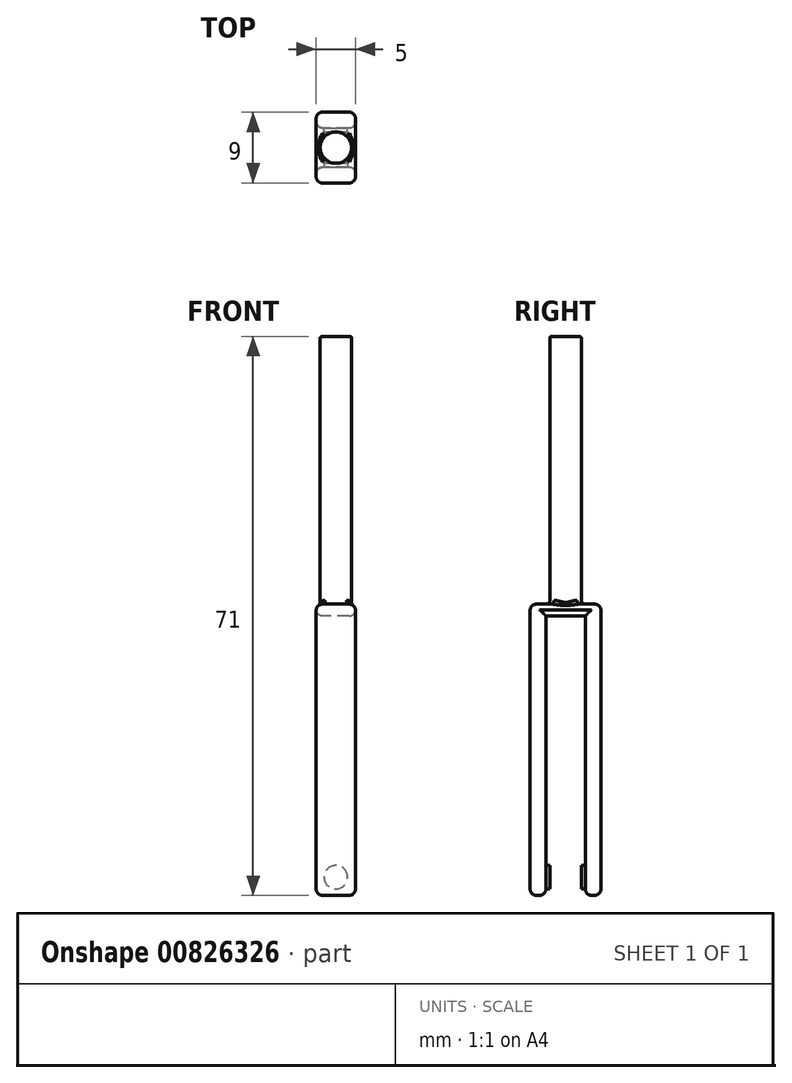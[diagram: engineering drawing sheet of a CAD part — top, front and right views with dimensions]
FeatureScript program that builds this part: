
annotation { "Feature Type Name" : "Feature", "Feature Type Description" : "" }
export const myFeature = defineFeature(function(context is Context, id is Id, definition is map)
    precondition{}
    {
        {
            var Q0;
            Q0=qCreatedBy(makeId("Front.planeOp"),FACE);
            var sketch = newSketch(context, id + "F0", { "sketchPlane" : qUnion([Q0])});
            skLineSegment(sketch, "E0", {"start": v(-41.6, 28) * mm, "end": v(-41.6, 0) * mm});
            skLineSegment(sketch, "E1", {"start": v(-36.6, 28) * mm, "end": v(-41.6, 28) * mm});
            skLineSegment(sketch, "E2", {"start": v(-41.6, 0) * mm, "end": v(-50.78, 0) * mm});
            skLineSegment(sketch, "E3", {"start": v(-41.6, 0) * mm, "end": v(-41.6, -9) * mm});
            skLineSegment(sketch, "E4", {"start": v(-41.6, -9) * mm, "end": v(-36.6, -9) * mm});
            skLineSegment(sketch, "E5", {"start": v(-36.6, -9) * mm, "end": v(-36.6, 28) * mm});
            skSolve(sketch);
        }
        {
            var Q0;
            Q0=makeQuery(id+"F0.imprint","IMPRINT",FACE,{"disambiguationData":[TD([[makeQuery(id+"F0.imprint","IMPRINT",EDGE,{"derivedFrom":sQuery(id+"F0.wireOp",EDGE,"E0")}),1.0]])]});
            extrude(context, id + "F1", {"entities" : qUnion([Q0]), "oppositeDirection" : true, "depth" : 2 * mm, "offsetDistance" : 25 * mm});
        }
        {
            var Q0;
            Q0=qCreatedBy(makeId("Front.planeOp"),FACE);
            cPlane(context, id + "F2", {"entities" : qUnion([Q0]), "cplaneType" : CPlaneType.OFFSET, "offset" : 2.5 * mm, "width" : 150 * mm, "height" : 150 * mm});
        }
        {
            var Q0;
            Q0=qCreatedBy(makeId("Top.planeOp"),FACE);
            cPlane(context, id + "F3", {"entities" : qUnion([Q0]), "cplaneType" : CPlaneType.OFFSET, "offset" : 27 * mm, "width" : 150 * mm, "height" : 150 * mm});
        }
        {
            var Q0;
            Q0=makeQuery(id+"F1.opExtrude","CAP_FACE",FACE,{"disambiguationData":[OSD([sQuery(id+"F0.wireOp",EDGE,"E0"),sQuery(id+"F0.wireOp",EDGE,"E1"),sQuery(id+"F0.wireOp",EDGE,"E3"),sQuery(id+"F0.wireOp",EDGE,"E4"),sQuery(id+"F0.wireOp",EDGE,"E5")])],"isStart":true});
            var sketch = newSketch(context, id + "F4", { "sketchPlane" : qUnion([Q0])});
            skPoint(sketch, "E6.trimOffspring.end.orphan", {"position": v(-36.6, -12.26) * mm});
            skPoint(sketch, "E7.start.orphan", {"position": v(-41.6, -10.83) * mm});
            skPoint(sketch, "E8.trimOffspring.end.orphan", {"position": v(-36.6, 30.02) * mm});
            skPoint(sketch, "E9.start.orphan", {"position": v(-41.6, 25.12) * mm});
            skPoint(sketch, "E10.center.orphan", {"position": v(-39.1, 27.57) * mm});
            skLineSegment(sketch, "E11.bottom", {"start": v(-36.6, 30.02) * mm, "end": v(-36.6, 30.02) * mm});
            skLineSegment(sketch, "E11.top", {"start": v(-36.6, 26.5) * mm, "end": v(-36.6, 26.5) * mm});
            skLineSegment(sketch, "E11.left", {"start": v(-36.6, 30.02) * mm, "end": v(-36.6, 26.5) * mm});
            skLineSegment(sketch, "E11.right", {"start": v(-36.6, 30.02) * mm, "end": v(-36.6, 26.5) * mm});
            skLineSegment(sketch, "E12.right", {"start": v(-41.6, 30.02) * mm, "end": v(-41.6, 30.02) * mm});
            skLineSegment(sketch, "E13.bottom", {"start": v(-41.6, 26.5) * mm, "end": v(-41.6, 26.5) * mm});
            skLineSegment(sketch, "E14", {"start": v(-41.6, 26.5) * mm, "end": v(-36.6, 26.5) * mm});
            skLineSegment(sketch, "E15", {"start": v(-36.6, 26.5) * mm, "end": v(-36.6, 28) * mm});
            skLineSegment(sketch, "E16", {"start": v(-36.6, 28) * mm, "end": v(-41.6, 28) * mm});
            skLineSegment(sketch, "E17", {"start": v(-41.6, 28) * mm, "end": v(-41.6, 26.5) * mm});
            skPoint(sketch, "E18.center.orphan", {"position": v(-39.1, -11.55) * mm});
            skCircle(sketch, "E19", {"center": v(-39.1, -6.69) * mm, "radius": 1.5 * mm});
            skPoint(sketch, "E20.orphan", {"position": v(-41.6, -6.69) * mm});
            skPoint(sketch, "E21.end.orphan", {"position": v(-36.6, -6.69) * mm});
            skSolve(sketch);
        }
        {
            var Q0;
            Q0=makeQuery(id+"F1.opExtrude","CAP_EDGE",EDGE,{"disambiguationData":[OSD([sQuery(id+"F0.wireOp",EDGE,"E5")])],"isStart":false});
            var Q1;
            Q1=makeQuery(id+"F1.opExtrude","CAP_EDGE",EDGE,{"disambiguationData":[OSD([sQuery(id+"F0.wireOp",EDGE,"E4")])],"isStart":false});
            var Q2;
            Q2=makeQuery(id+"F1.opExtrude","CAP_EDGE",EDGE,{"disambiguationData":[OSD([sQuery(id+"F0.wireOp",EDGE,"E4")])],"isStart":true});
            var Q3;
            Q3=makeQuery(id+"F1.opExtrude","CAP_EDGE",EDGE,{"disambiguationData":[OSD([sQuery(id+"F0.wireOp",EDGE,"E5")])],"isStart":true});
            var Q4;
            Q4=makeQuery(id+"F1.opExtrude","CAP_EDGE",EDGE,{"disambiguationData":[OSD([sQuery(id+"F0.wireOp",EDGE,"E0"),sQuery(id+"F0.wireOp",EDGE,"E3")])],"isStart":true});
            var Q5;
            Q5=makeQuery(id+"F1.opExtrude","CAP_EDGE",EDGE,{"disambiguationData":[OSD([sQuery(id+"F0.wireOp",EDGE,"E0"),sQuery(id+"F0.wireOp",EDGE,"E3")])],"isStart":false});
            var Q6;
            Q6=makeQuery(id+"F1.opExtrude","CAP_EDGE",EDGE,{"disambiguationData":[OSD([sQuery(id+"F0.wireOp",EDGE,"E1")])],"isStart":false});
            var Q7;
            Q7=makeQuery(id+"F1.opExtrude","CAP_EDGE",EDGE,{"disambiguationData":[OSD([sQuery(id+"F0.wireOp",EDGE,"E1")])],"isStart":true});
            var Q8;
            Q8=makeQuery(id+"F1.opExtrude","SWEPT_EDGE",EDGE,{"disambiguationData":[OSD([sQuery(id+"F0.wireOp",EDGE,"E0"),sQuery(id+"F0.wireOp",EDGE,"E1")])]});
            var Q9;
            Q9=makeQuery(id+"F1.opExtrude","SWEPT_EDGE",EDGE,{"disambiguationData":[OSD([sQuery(id+"F0.wireOp",EDGE,"E1"),sQuery(id+"F0.wireOp",EDGE,"E5")])]});
            var Q10;
            Q10=makeQuery(id+"F1.opExtrude","SWEPT_EDGE",EDGE,{"disambiguationData":[OSD([sQuery(id+"F0.wireOp",EDGE,"E4"),sQuery(id+"F0.wireOp",EDGE,"E5")])]});
            var Q11;
            Q11=makeQuery(id+"F1.opExtrude","SWEPT_EDGE",EDGE,{"disambiguationData":[OSD([sQuery(id+"F0.wireOp",EDGE,"E3"),sQuery(id+"F0.wireOp",EDGE,"E4")])]});
            fillet(context, id + "F5", {"entities" : qUnion([Q0, Q1, Q2, Q3, Q4, Q5, Q6, Q7, Q8, Q9, Q10, Q11]), "radius" : 0.8 * mm, "tangentPropagation" : true, "allowEdgeOverflow" : false});
        }
        {
            var Q0;
            Q0=makeQuery(id+"F1.opExtrude","SWEPT_BODY",BODY,{"disambiguationData":[OSD([sQuery(id+"F0.wireOp",EDGE,"E0"),sQuery(id+"F0.wireOp",EDGE,"E1"),sQuery(id+"F0.wireOp",EDGE,"E3"),sQuery(id+"F0.wireOp",EDGE,"E4"),sQuery(id+"F0.wireOp",EDGE,"E5")])]});
            var Q1;
            Q1=qCreatedBy(id+"F2.planeOp",FACE);
            mirror(context, id + "F6", {"operationType" : NewBodyOperationType.ADD, "entities" : qUnion([Q0]), "mirrorPlane" : qUnion([Q1])});
        }
        {
            var Q0;
            Q0=makeQuery(id+"F4.imprint","IMPRINT",FACE,{"disambiguationData":[TD([[makeQuery(id+"F4.imprint","IMPRINT",EDGE,{"derivedFrom":sQuery(id+"F4.wireOp",EDGE,"E14")}),1.0]])]});
            extrude(context, id + "F7", {"entities" : qUnion([Q0]), "depth" : 6 * mm, "offsetDistance" : 25 * mm});
        }
        {
            var Q0;
            Q0=makeQuery(id+"F7.opExtrude","SWEPT_BODY",BODY,{"disambiguationData":[OSD([sQuery(id+"F4.wireOp",EDGE,"E14"),sQuery(id+"F4.wireOp",EDGE,"E15"),sQuery(id+"F4.wireOp",EDGE,"E16"),sQuery(id+"F4.wireOp",EDGE,"E17")])]});
            var Q1;
            Q1=qCreatedBy(id+"F2.planeOp",FACE);
            mirror(context, id + "F8", {"entities" : qUnion([Q0]), "mirrorPlane" : qUnion([Q1])});
        }
        {
            var Q0;
            Q0=makeQuery(id+"F7.opExtrude","SWEPT_BODY",BODY,{"disambiguationData":[OSD([sQuery(id+"F4.wireOp",EDGE,"E14"),sQuery(id+"F4.wireOp",EDGE,"E15"),sQuery(id+"F4.wireOp",EDGE,"E16"),sQuery(id+"F4.wireOp",EDGE,"E17")])]});
            var Q1;
            Q1=makeQuery(id+"F8.opPattern","COPY",BODY,{"derivedFrom":makeQuery(id+"F7.opExtrude","SWEPT_BODY",BODY,{"disambiguationData":[OSD([sQuery(id+"F4.wireOp",EDGE,"E14"),sQuery(id+"F4.wireOp",EDGE,"E15"),sQuery(id+"F4.wireOp",EDGE,"E16"),sQuery(id+"F4.wireOp",EDGE,"E17")])]}),"instanceName":"1"});
            booleanBodies(context, id + "F9", {"operationType" : BooleanOperationType.UNION, "tools" : qUnion([Q0, Q1])});
        }
        {
            var Q0;
            {var subQ0=makeQuery(id+"F7.opExtrude","SWEPT_EDGE",EDGE,{"disambiguationData":[OSD([sQuery(id+"F4.wireOp",EDGE,"E16"),sQuery(id+"F4.wireOp",EDGE,"E17")])]});Q0=makeQuery(id+"F9.opBoolean","MERGE",EDGE,{"derivedFrom":[subQ0,makeQuery(id+"F8.opPattern","COPY",EDGE,{"derivedFrom":subQ0,"instanceName":"1"})]});}
            var Q1;
            {var subQ0=makeQuery(id+"F7.opExtrude","SWEPT_EDGE",EDGE,{"disambiguationData":[OSD([sQuery(id+"F0.wireOp",EDGE,"E0"),sQuery(id+"F0.wireOp",EDGE,"E3"),sQuery(id+"F4.wireOp",EDGE,"E14"),sQuery(id+"F4.wireOp",EDGE,"E17")])]});Q1=makeQuery(id+"F9.opBoolean","MERGE",EDGE,{"derivedFrom":[subQ0,makeQuery(id+"F8.opPattern","COPY",EDGE,{"derivedFrom":subQ0,"instanceName":"1"})]});}
            var Q2;
            {var subQ0=makeQuery(id+"F7.opExtrude","SWEPT_EDGE",EDGE,{"disambiguationData":[OSD([sQuery(id+"F0.wireOp",EDGE,"E5"),sQuery(id+"F4.wireOp",EDGE,"E14"),sQuery(id+"F4.wireOp",EDGE,"E15")])]});Q2=makeQuery(id+"F9.opBoolean","MERGE",EDGE,{"derivedFrom":[subQ0,makeQuery(id+"F8.opPattern","COPY",EDGE,{"derivedFrom":subQ0,"instanceName":"1"})]});}
            var Q3;
            {var subQ0=makeQuery(id+"F7.opExtrude","SWEPT_EDGE",EDGE,{"disambiguationData":[OSD([sQuery(id+"F4.wireOp",EDGE,"E15"),sQuery(id+"F4.wireOp",EDGE,"E16")])]});Q3=makeQuery(id+"F9.opBoolean","MERGE",EDGE,{"derivedFrom":[subQ0,makeQuery(id+"F8.opPattern","COPY",EDGE,{"derivedFrom":subQ0,"instanceName":"1"})]});}
            fillet(context, id + "F10", {"entities" : qUnion([Q0, Q1, Q2, Q3]), "radius" : 0.8 * mm, "tangentPropagation" : true, "allowEdgeOverflow" : false});
        }
        {
            var Q0;
            Q0=makeQuery(id+"F1.opExtrude","SWEPT_BODY",BODY,{"disambiguationData":[OSD([sQuery(id+"F0.wireOp",EDGE,"E0"),sQuery(id+"F0.wireOp",EDGE,"E1"),sQuery(id+"F0.wireOp",EDGE,"E3"),sQuery(id+"F0.wireOp",EDGE,"E4"),sQuery(id+"F0.wireOp",EDGE,"E5")])]});
            var Q1;
            Q1=makeQuery(id+"F6.opPattern","COPY",BODY,{"derivedFrom":makeQuery(id+"F1.opExtrude","SWEPT_BODY",BODY,{"disambiguationData":[OSD([sQuery(id+"F0.wireOp",EDGE,"E0"),sQuery(id+"F0.wireOp",EDGE,"E1"),sQuery(id+"F0.wireOp",EDGE,"E3"),sQuery(id+"F0.wireOp",EDGE,"E4"),sQuery(id+"F0.wireOp",EDGE,"E5")])]}),"instanceName":"1"});
            var Q2;
            Q2=makeQuery(id+"F7.opExtrude","SWEPT_BODY",BODY,{"disambiguationData":[OSD([sQuery(id+"F4.wireOp",EDGE,"E14"),sQuery(id+"F4.wireOp",EDGE,"E15"),sQuery(id+"F4.wireOp",EDGE,"E16"),sQuery(id+"F4.wireOp",EDGE,"E17")])]});
            booleanBodies(context, id + "F11", {"operationType" : BooleanOperationType.UNION, "tools" : qUnion([Q0, Q1, Q2])});
        }
        {
            var Q0;
            Q0=makeQuery(id+"F4.imprint","IMPRINT",FACE,{"disambiguationData":[TD([[makeQuery(id+"F4.imprint","IMPRINT",EDGE,{"derivedFrom":sQuery(id+"F4.wireOp",EDGE,"E19")}),1.0]])]});
            extrude(context, id + "F12", {"entities" : qUnion([Q0]), "operationType" : NewBodyOperationType.ADD, "depth" : 0.5 * mm, "offsetDistance" : 25 * mm});
        }
        {
            var Q0;
            Q0=makeQuery(id+"F1.opExtrude","SWEPT_BODY",BODY,{"disambiguationData":[OSD([sQuery(id+"F0.wireOp",EDGE,"E0"),sQuery(id+"F0.wireOp",EDGE,"E1"),sQuery(id+"F0.wireOp",EDGE,"E3"),sQuery(id+"F0.wireOp",EDGE,"E4"),sQuery(id+"F0.wireOp",EDGE,"E5")])]});
            var Q1;
            Q1=qCreatedBy(id+"F2.planeOp",FACE);
            mirror(context, id + "F13", {"operationType" : NewBodyOperationType.ADD, "entities" : qUnion([Q0]), "mirrorPlane" : qUnion([Q1])});
        }
        {
            var Q0;
            Q0=qCreatedBy(id+"F3.planeOp",FACE);
            var sketch = newSketch(context, id + "F14", { "sketchPlane" : qUnion([Q0])});
            skCircle(sketch, "E22", {"center": v(-39.1, -2.5) * mm, "radius": 2 * mm});
            skPoint(sketch, "E23.trimOffspring.end.orphan", {"position": v(-39.1, -6.2) * mm});
            skPoint(sketch, "E24.trimOffspring.end.orphan", {"position": v(-40.8, -6.2) * mm});
            skPoint(sketch, "E25.orphan", {"position": v(-41.6, -6.2) * mm});
            skPoint(sketch, "E26.start.orphan", {"position": v(-39.1, 1.2) * mm});
            skPoint(sketch, "E27.0.2.end.orphan", {"position": v(-41.6, 1.2) * mm});
            skPoint(sketch, "E28.0.2.end.orphan", {"position": v(-37.4, 1.2) * mm});
            skPoint(sketch, "E29.orphan", {"position": v(-36.6, 1.2) * mm});
            skPoint(sketch, "E28.0.1.start.orphan", {"position": v(-36.6, -6.2) * mm});
            skPoint(sketch, "E28.0.3.start.orphan", {"position": v(-37.4, -6.2) * mm});
            skPoint(sketch, "E30.trimOffspring.end.orphan", {"position": v(-40.8, 1.2) * mm});
            skSolve(sketch);
        }
        {
            var Q0;
            Q0 = qSketchRegion(id + "F14", true);
            extrude(context, id + "F15", {"entities" : qUnion([Q0]), "operationType" : NewBodyOperationType.ADD, "depth" : 35 * mm, "offsetDistance" : 25 * mm});
        }
        {
            var Q0;
            {var subQ0=sQuery(id+"F0.wireOp",EDGE,"E5");var subQ1=sQuery(id+"F0.wireOp",EDGE,"E1");var subQ2=makeQuery(id+"F5.opFillet","BLEND_FACE",FACE,{"disambiguationData":[OSD([subQ1,subQ0]),TDD([makeQuery(id+"F1.opExtrude","SWEPT_EDGE",EDGE,{"disambiguationData":[OSD([subQ1,subQ0])]})])]});Q0=makeQuery(id+"F15.boolean.opBoolean","INTERSECT",EDGE,{"derivedFrom":[makeQuery(id+"F11.opBoolean","MERGE",FACE,{"derivedFrom":[subQ2,makeQuery(id+"F6.opPattern","COPY",FACE,{"derivedFrom":subQ2,"instanceName":"1"}),makeQuery(id+"F10.opFillet","BLEND_FACE",FACE,{"disambiguationData":[OSD([sQuery(id+"F4.wireOp",EDGE,"E15"),sQuery(id+"F4.wireOp",EDGE,"E16")])]})]}),makeQuery(id+"F15.opExtrude","SWEPT_FACE",FACE,{"disambiguationData":[OSD([sQuery(id+"F14.wireOp",EDGE,"E22")])]})]});}
            var Q1;
            {var subQ1=sQuery(id+"F0.wireOp",EDGE,"E1");var subQ5=sQuery(id+"F4.wireOp",EDGE,"E16");var subQ6=makeQuery(id+"F7.opExtrude","SWEPT_FACE",FACE,{"disambiguationData":[OSD([subQ5])]});var subQ7=makeQuery(id+"F1.opExtrude","SWEPT_FACE",FACE,{"disambiguationData":[OSD([subQ1])]});Q1=makeQuery(id+"F15.boolean.opBoolean","SPLIT",FACE,{"disambiguationData":[TD([makeQuery(id+"F15.opExtrude","SWEPT_FACE",FACE,{"disambiguationData":[OSD([sQuery(id+"F14.wireOp",EDGE,"E22")])]})])],"derivedFrom":makeQuery(id+"F11.opBoolean","MERGE",FACE,{"derivedFrom":[subQ7,makeQuery(id+"F6.opPattern","COPY",FACE,{"derivedFrom":subQ7,"instanceName":"1"}),makeQuery(id+"F9.opBoolean","MERGE",FACE,{"derivedFrom":[subQ6,makeQuery(id+"F8.opPattern","COPY",FACE,{"derivedFrom":subQ6,"instanceName":"1"})]})]})});}
            fillet(context, id + "F16", {"entities" : qUnion([Q0, Q1]), "radius" : 0.5 * mm, "tangentPropagation" : true, "allowEdgeOverflow" : false});
        }
        {
            var Q0;
            Q0=makeQuery(id+"F15.opExtrude","CAP_FACE",FACE,{"disambiguationData":[OSD([sQuery(id+"F14.wireOp",EDGE,"iyl9hkM8-ck8G-q8f9-TtUS-YjyyFDmVukht"),sQuery(id+"F14.wireOp",EDGE,"E22")])],"isStart":false});
            fillet(context, id + "F17", {"entities" : qUnion([Q0]), "radius" : 0.2 * mm, "tangentPropagation" : true, "allowEdgeOverflow" : false});
        }
    });
